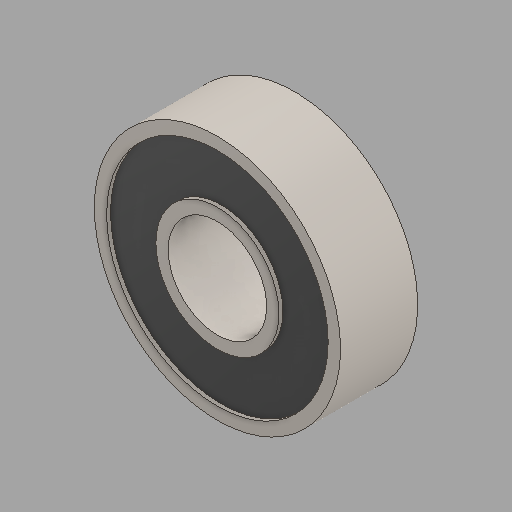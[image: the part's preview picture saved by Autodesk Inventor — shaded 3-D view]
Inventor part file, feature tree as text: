
AUTODESK INVENTOR PART (.ipt)
format: ipt  version: 2024.2 (Build 282272000, 272)  size: 134,144 bytes
history: native  units: in
note: dims shown in document units (in); Inventor stores cm internally (conversion verified against a paired STEP export)
features: revolve x1
ambient origin geometry x8: Origin, YZ Plane, XZ Plane, XY Plane, X Axis, Y Axis, Z Axis, Center Point
bodies: Solid1 (feature_tree)
feature tree (1):
  revolve  "Revolve1"  [1 undecoded]
note: 1 required parameter value undecoded (feature->parameter linkage not recoverable at this tier; creation-order binding heuristic only, values carry confidence <= 0.55)
